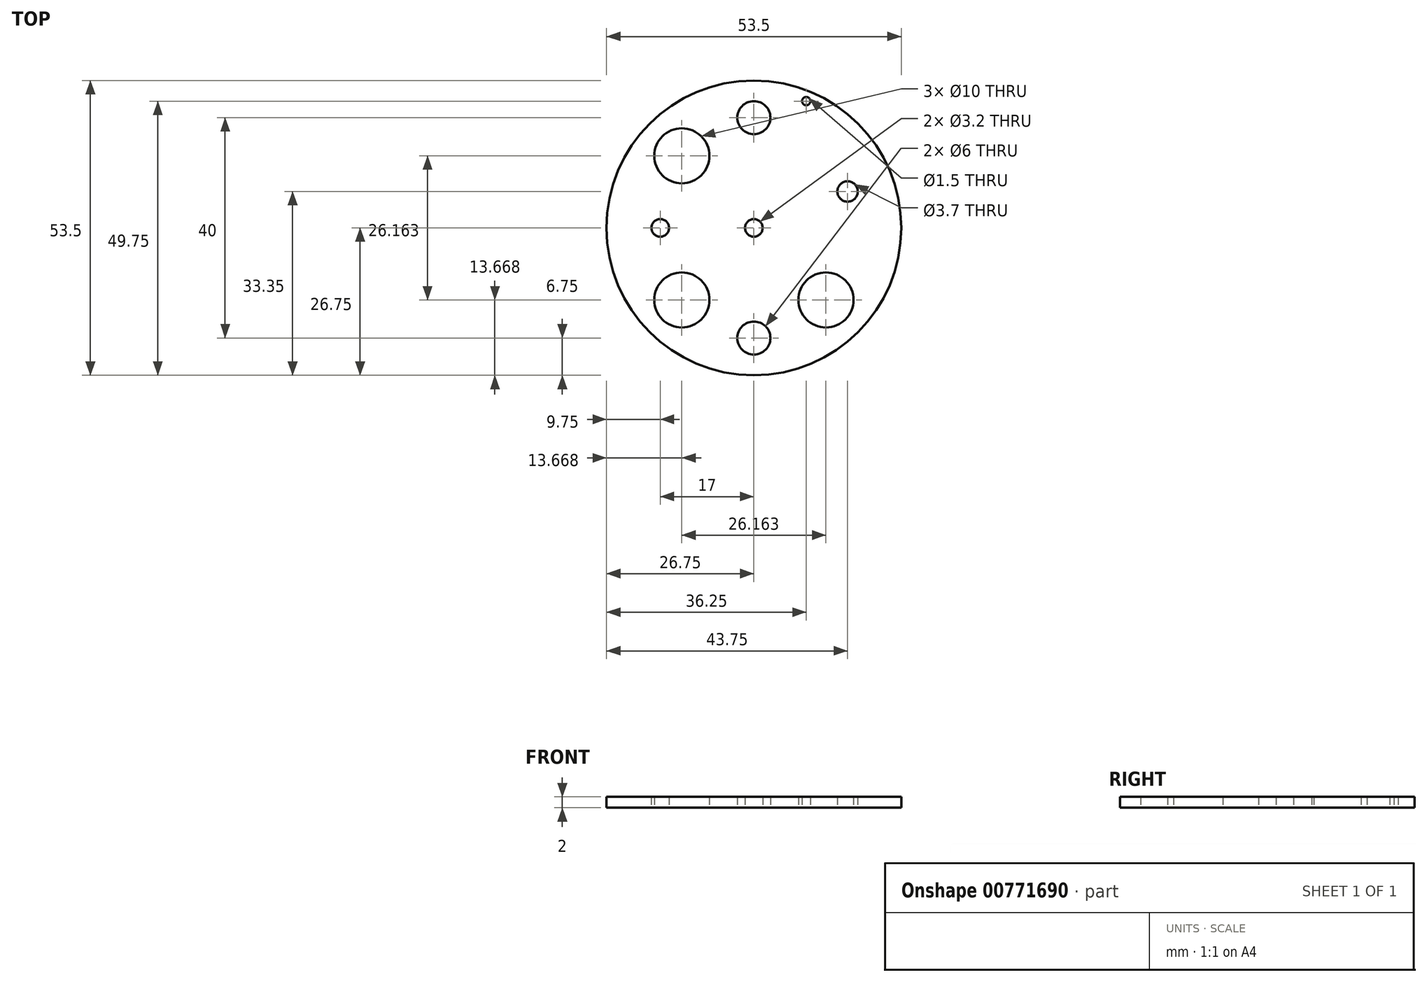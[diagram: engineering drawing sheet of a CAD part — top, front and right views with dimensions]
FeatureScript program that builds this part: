
annotation { "Feature Type Name" : "Feature", "Feature Type Description" : "" }
export const myFeature = defineFeature(function(context is Context, id is Id, definition is map)
    precondition{}
    {
        {
            var Q0;
            Q0=qCreatedBy(makeId("Top.planeOp"),FACE);
            var sketch = newSketch(context, id + "F0", { "sketchPlane" : qUnion([Q0])});
            skCircle(sketch, "E0", {"center": v(0, 0) * mm, "radius": 26.75 * mm});
            skLineSegment(sketch, "E1.bottom", {"start": v(13.08, 13.08) * mm, "end": v(-13.08, 13.08) * mm});
            skLineSegment(sketch, "E1.top", {"start": v(13.08, -13.08) * mm, "end": v(-13.08, -13.08) * mm});
            skLineSegment(sketch, "E1.left", {"start": v(13.08, 13.08) * mm, "end": v(13.08, -13.08) * mm});
            skLineSegment(sketch, "E1.right", {"start": v(-13.08, 13.08) * mm, "end": v(-13.08, -13.08) * mm});
            skCircle(sketch, "E2", {"center": v(-13.08, 13.08) * mm, "radius": 5 * mm});
            skCircle(sketch, "E3", {"center": v(-13.08, -13.08) * mm, "radius": 5 * mm});
            skCircle(sketch, "E4", {"center": v(13.08, -13.08) * mm, "radius": 5 * mm});
            skPoint(sketch, "E5", {"position": v(0, -20) * mm});
            skPoint(sketch, "E6", {"position": v(0, 20) * mm});
            skCircle(sketch, "E7", {"center": v(0, 20) * mm, "radius": 3 * mm});
            skCircle(sketch, "E8", {"center": v(0, -20) * mm, "radius": 3 * mm});
            skCircle(sketch, "E9", {"center": v(-17, 0) * mm, "radius": 1.6 * mm});
            skCircle(sketch, "E10", {"center": v(17, 6.6) * mm, "radius": 1.85 * mm});
            skCircle(sketch, "E11", {"center": v(0, 0) * mm, "radius": 1.6 * mm});
            skCircle(sketch, "E12", {"center": v(9.5, 23) * mm, "radius": 0.75 * mm});
            skSolve(sketch);
        }
        {
            var Q0;
            Q0=makeQuery(id+"F0.imprint","IMPRINT",FACE,{"disambiguationData":[TD([[makeQuery(id+"F0.imprint","IMPRINT",EDGE,{"derivedFrom":sQuery(id+"F0.wireOp",EDGE,"E0")}),1.0]])]});
            var Q1;
            Q1=makeQuery(id+"F0.imprint","IMPRINT",FACE,{"disambiguationData":[TD([[makeQuery(id+"F0.imprint","IMPRINT",EDGE,{"derivedFrom":sQuery(id+"F0.wireOp",EDGE,"68873bf2-f16a-4f8c-a10e-2667304634ca")}),-1.0]])]});
            var Q2;
            Q2=makeQuery(id+"F0.imprint","IMPRINT",FACE,{"disambiguationData":[TD([[makeQuery(id+"F0.imprint","IMPRINT",EDGE,{"derivedFrom":sQuery(id+"F0.wireOp",EDGE,"E11")}),-1.0]])]});
            extrude(context, id + "F1", {"entities" : qUnion([Q0, Q1, Q2]), "depth" : 2 * mm, "offsetDistance" : 25 * mm});
        }
    });
